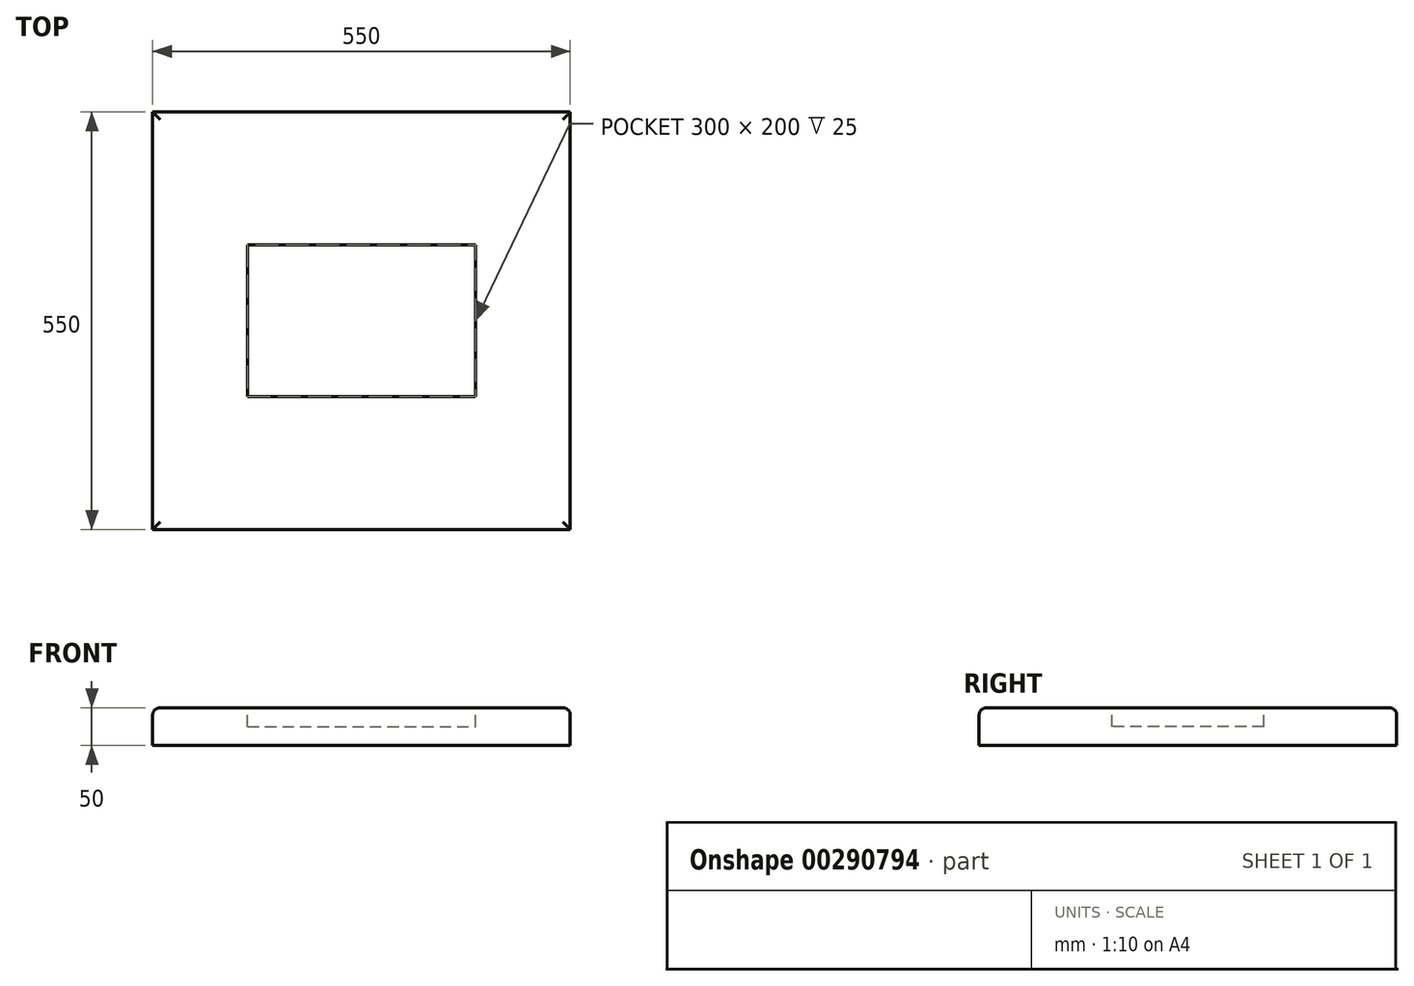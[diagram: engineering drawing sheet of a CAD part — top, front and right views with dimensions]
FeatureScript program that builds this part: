
annotation { "Feature Type Name" : "Feature", "Feature Type Description" : "" }
export const myFeature = defineFeature(function(context is Context, id is Id, definition is map)
    precondition{}
    {
        {
            var Q0;
            Q0=qCreatedBy(makeId("Top.planeOp"),FACE);
            var sketch = newSketch(context, id + "F0", { "sketchPlane" : qUnion([Q0])});
            skPoint(sketch, "E0.middle", {"position": v(0, 0) * mm});
            skLineSegment(sketch, "E1.bottom", {"start": v(275, -275) * mm, "end": v(-275, -275) * mm});
            skLineSegment(sketch, "E1.top", {"start": v(275, 275) * mm, "end": v(-275, 275) * mm});
            skLineSegment(sketch, "E1.left", {"start": v(275, -275) * mm, "end": v(275, 275) * mm});
            skLineSegment(sketch, "E1.right", {"start": v(-275, -275) * mm, "end": v(-275, 275) * mm});
            skSolve(sketch);
        }
        {
            var Q0;
            Q0=makeQuery(id+"F0.imprint","IMPRINT",FACE,{"disambiguationData":[TD([[makeQuery(id+"F0.imprint","IMPRINT",EDGE,{"derivedFrom":sQuery(id+"F0.wireOp",EDGE,"E1.bottom")}),-1.0]])]});
            extrude(context, id + "F1", {"entities" : qUnion([Q0]), "depth" : 50 * mm});
        }
        {
            var Q0;
            Q0=makeQuery(id+"F1.opExtrude","CAP_EDGE",EDGE,{"disambiguationData":[OSD([sQuery(id+"F0.wireOp",EDGE,"E1.right")])],"isStart":false});
            var Q1;
            Q1=makeQuery(id+"F1.opExtrude","CAP_EDGE",EDGE,{"disambiguationData":[OSD([sQuery(id+"F0.wireOp",EDGE,"E1.top")])],"isStart":false});
            var Q2;
            Q2=makeQuery(id+"F1.opExtrude","CAP_EDGE",EDGE,{"disambiguationData":[OSD([sQuery(id+"F0.wireOp",EDGE,"E1.left")])],"isStart":false});
            var Q3;
            Q3=makeQuery(id+"F1.opExtrude","CAP_EDGE",EDGE,{"disambiguationData":[OSD([sQuery(id+"F0.wireOp",EDGE,"E1.bottom")])],"isStart":false});
            fillet(context, id + "F2", {"entities" : qUnion([Q0, Q1, Q2, Q3]), "radius" : 10 * mm, "tangentPropagation" : true, "allowEdgeOverflow" : false});
        }
        {
            var Q0;
            Q0=makeQuery(id+"F1.opExtrude","CAP_FACE",FACE,{"disambiguationData":[OSD([sQuery(id+"F0.wireOp",EDGE,"E1.bottom"),sQuery(id+"F0.wireOp",EDGE,"E1.top"),sQuery(id+"F0.wireOp",EDGE,"E1.left"),sQuery(id+"F0.wireOp",EDGE,"E1.right")])],"isStart":false});
            var sketch = newSketch(context, id + "F3", { "sketchPlane" : qUnion([Q0])});
            skLineSegment(sketch, "E2.bottom", {"start": v(-150, 100) * mm, "end": v(150, 100) * mm});
            skLineSegment(sketch, "E2.top", {"start": v(-150, -100) * mm, "end": v(150, -100) * mm});
            skLineSegment(sketch, "E2.left", {"start": v(-150, 100) * mm, "end": v(-150, -100) * mm});
            skLineSegment(sketch, "E2.right", {"start": v(150, 100) * mm, "end": v(150, -100) * mm});
            skPoint(sketch, "E2.middle", {"position": v(0, 0) * mm});
            skSolve(sketch);
        }
        {
            var Q0;
            Q0=makeQuery(id+"F3.imprint","IMPRINT",FACE,{"disambiguationData":[TD([[makeQuery(id+"F3.imprint","IMPRINT",EDGE,{"derivedFrom":sQuery(id+"F3.wireOp",EDGE,"E2.bottom")}),-1.0]])]});
            extrude(context, id + "F4", {"entities" : qUnion([Q0]), "operationType" : NewBodyOperationType.ADD, "oppositeDirection" : true, "depth" : 25 * mm});
        }
        {
            var Q0;
            Q0=makeQuery(id+"F3.imprint","IMPRINT",FACE,{"disambiguationData":[TD([[makeQuery(id+"F3.imprint","IMPRINT",EDGE,{"derivedFrom":sQuery(id+"F3.wireOp",EDGE,"E2.bottom")}),-1.0]])]});
            extrude(context, id + "F5", {"entities" : qUnion([Q0]), "operationType" : NewBodyOperationType.REMOVE, "oppositeDirection" : true, "depth" : 25 * mm});
        }
    });
